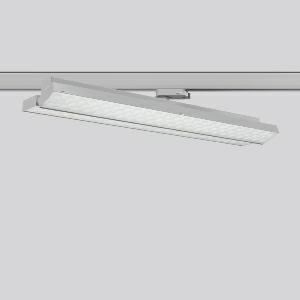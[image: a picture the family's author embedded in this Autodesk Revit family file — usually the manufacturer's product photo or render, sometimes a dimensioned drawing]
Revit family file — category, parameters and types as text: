
# Revit family: tx-move_742163_004_2_76_8108
name_source: partatom
category: Lighting Fixtures
units: mm (PartAtom-declared; Revit-internal decimal feet)

## family parameters
Cut with Voids When Loaded = No
Host = Face
Light Source = No
Part Type = Normal
Room Calculation Point = No
Round Connector Dimension = Use Diameter
Shared = No

## types (1)
- MultiLumen 1 (1 x LED Modul 927, 1975 lm, 2700)
    Apparent Load = 38 VA
    CIE Flux Codes = 65 90 98 100 100
    Color Rendering = 92
    Color Temperature = 2700
    Default Elevation = 1800 mm
    Description = Series: TX-MOVE
Multifunctional surface-mounted spotlight for area lighting. Very flat design. Housing: sheet steel, powder-coated. Rotation range: 356°. Swivel range: 90°. Consistent alignment possible with visible tilt scale. High-efficiency LED units with optimum light control thanks to clear plastic (PC) lens optics. Spezielle Mikrostrukturen reduzieren Gelbsaum. Asymmetrical light distribution. Best colour rendering with CRI >90 for fresh products and coloured textiles. With adapter for RZB 3-circuit DALI tracks. Suitable for Track on ceiling. MultiLumen: Luminous flux adjustable in 3 steps. Factory setting is the highest luminous flux. Environmentally friendly and resource-saving due to replaceable and recyclable components. 
Colour: silver, matt (approx. RAL 9006)
Length: 570 mm
Width: 119 mm
Height: 88 mm
Lamp: LED
Socket: without socket
Colour temperature: 2700K
Colour rendering index (CRI): 90
System power: 38 W
Rated luminous flux: 3950 lm
Luminous efficiency: 104 lm/W
System power 2: 51 W
Rated luminous flux 2: 5150 lm
Luminous efficiency 2: 101 lm/W
System power 3: 62 W
Rated luminous flux 3: 6150 lm
Luminous efficiency 3: 99 lm/W
Control gear: Dimmable EVG, DALI
Protection class: I
Type of protection: IP 20
    Height = 75 mm
    Lamp = 1 x LED Modul 927
    Lamp Light Flux = 1975 lm
    Lamp count = 1
    Length = 569 mm
    Lifetime = 50000 h
    Luminous efficacy = 104 lm/W
    Manufacturer = RZB
    ModVariant = No
    Model = 742163.004.2.76
    Mounting Place = Ceiling
    Mounting Type = Surface mounted
    Number of Poles = 1
    OnlyDefault = Yes
    Power Factor = 1
    Product Name = TX-MOVE
    Product group = Track mounted projectors
    ProductGroupID = 301
    Protection Class = Protection class I
    Protection Degree = IP 20
    RLX_Detail_Level = 1
    RLX_Emergency_Light_Flux = 0 lm
    RLX_Emergency_Type = 0
    RLX_Emergency_Type_DB = No
    RlxData = <blob elided: 53901 chars, md5=65328bf7>
    Socket = socket
    Standby Power = 0 W
    System Light Flux = 3950 lm
    System Power = 38 W
    Type Comments = MultiLumen 1
    Type Image = 742162.004.jpg
    URL = http://relux.com
    VarID = multilumen_1
    Voltage = 0 V
    Weight = 0.00 kg
    Width = 119 mm

## geometry (parser evidence)
native form markers: Blend x4, Sweep x17
no freeform markers — native parametric forms only
